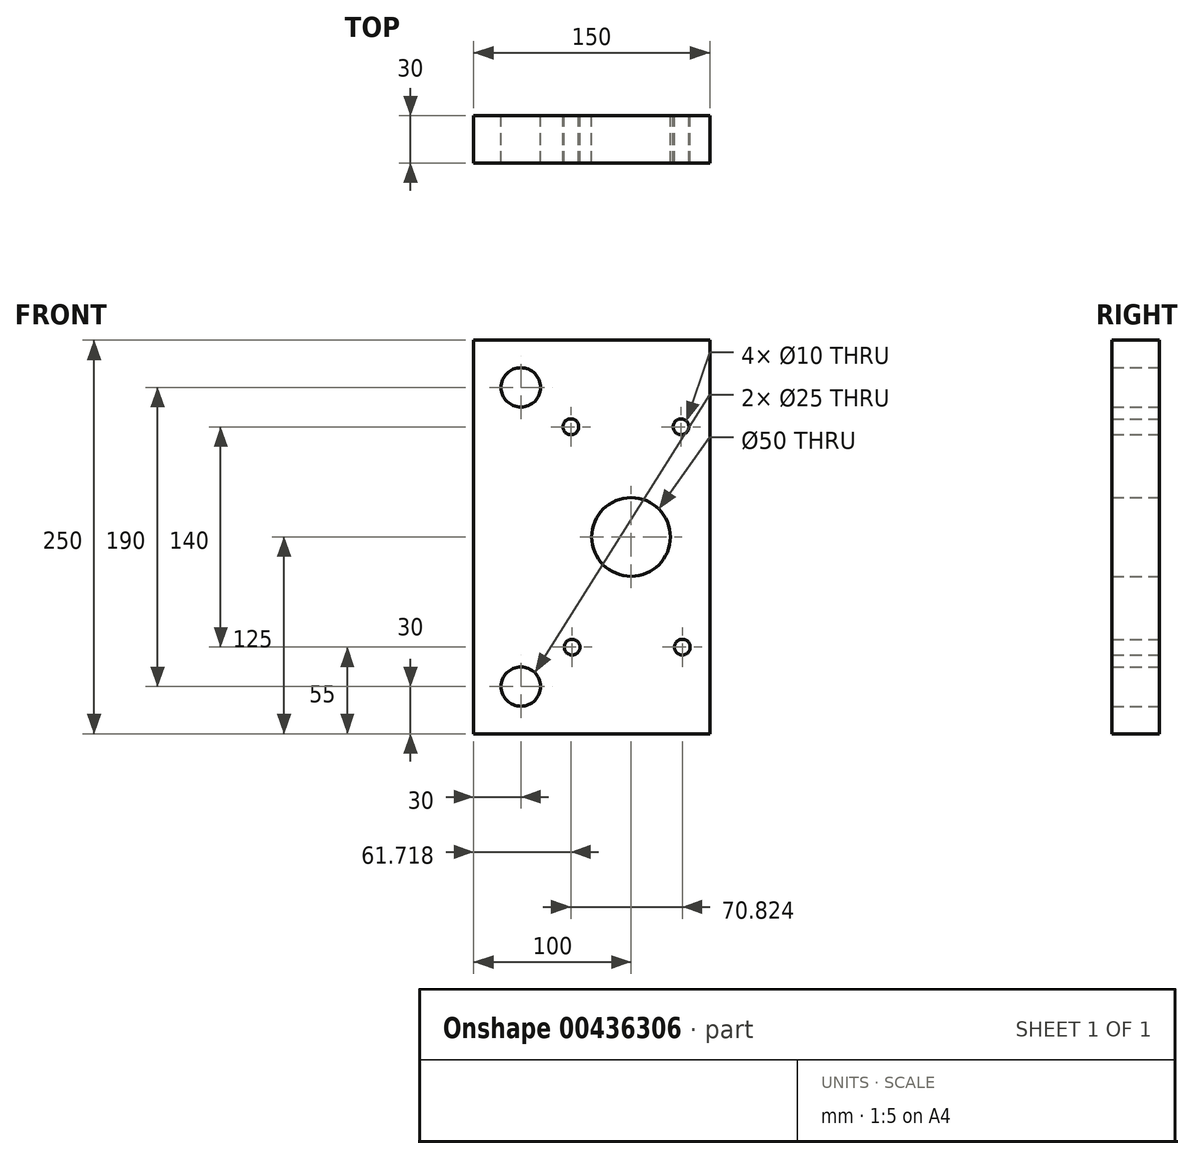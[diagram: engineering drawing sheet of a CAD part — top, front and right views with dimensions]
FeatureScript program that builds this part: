
annotation { "Feature Type Name" : "Feature", "Feature Type Description" : "" }
export const myFeature = defineFeature(function(context is Context, id is Id, definition is map)
    precondition{}
    {
        {
            var Q0;
            Q0=qCreatedBy(makeId("Front.planeOp"),FACE);
            var sketch = newSketch(context, id + "F0", { "sketchPlane" : qUnion([Q0])});
            skLineSegment(sketch, "E0.bottom", {"start": v(75, 125) * mm, "end": v(-75, 125) * mm});
            skLineSegment(sketch, "E0.top", {"start": v(75, -125) * mm, "end": v(-75, -125) * mm});
            skLineSegment(sketch, "E0.left", {"start": v(75, 125) * mm, "end": v(75, -125) * mm});
            skLineSegment(sketch, "E0.right", {"start": v(-75, 125) * mm, "end": v(-75, -125) * mm});
            skPoint(sketch, "E0.middle", {"position": v(0, 0) * mm});
            skCircle(sketch, "E1", {"center": v(25, 0) * mm, "radius": 25 * mm});
            skLineSegment(sketch, "E2", {"start": v(75, -125) * mm, "end": v(75, -70) * mm});
            skCircle(sketch, "E3", {"center": v(57.54, -70) * mm, "radius": 5 * mm});
            skCircle(sketch, "E4", {"center": v(-12.46, -70) * mm, "radius": 5 * mm});
            skCircle(sketch, "E5", {"center": v(56.72, 70) * mm, "radius": 5 * mm});
            skCircle(sketch, "E6", {"center": v(-13.28, 70) * mm, "radius": 5 * mm});
            skCircle(sketch, "E7", {"center": v(-45, -95) * mm, "radius": 12.5 * mm});
            skCircle(sketch, "E8", {"center": v(-45, 95) * mm, "radius": 12.5 * mm});
            skSolve(sketch);
        }
        {
            var Q0;
            Q0 = qSketchRegion(id + "F0", true);
            extrude(context, id + "F1", {"entities" : qUnion([Q0]), "depth" : 30 * mm});
        }
    });
